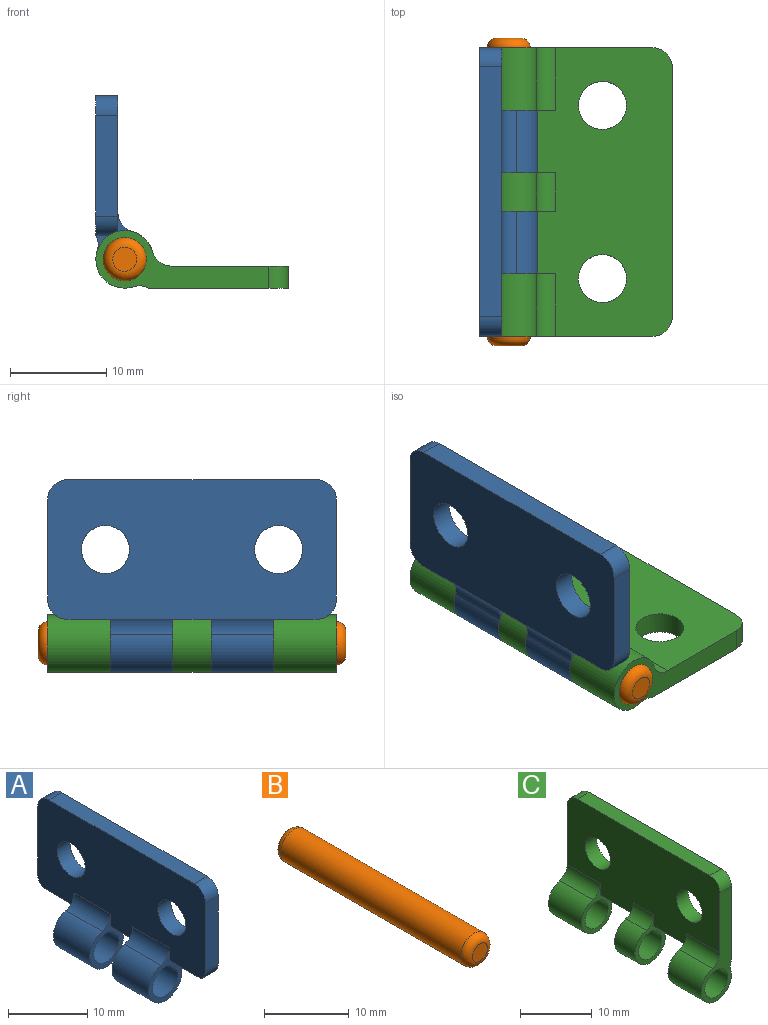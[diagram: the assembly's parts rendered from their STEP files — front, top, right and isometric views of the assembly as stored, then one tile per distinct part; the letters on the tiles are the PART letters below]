
ASSEMBLY  parts=3 mates=4
PART A: 29 faces, bbox 6x30x20 mm
  f0: plane 30x14.5mm, normal (1,0,0), area 392.3mm2, adj f2,f3,f8,f9,f10,f11,f20,f22
  f1: plane 30x14.08mm, normal (-1,0,0), area 355.9mm2, adj f8,f9,f10,f12,f13,f14,f15,f16
  f2: plane 4x1.34mm, normal (0,0,-1), area 5.4mm2, adj f0,f12,f13,f14
  f3: plane 4.5x1.34mm, normal (0,0,-1), area 6mm2, adj f0,f15,f16,f25
  f4: cylinder r=3mm len=6.5mm, axis (0,1,0), area 92.9mm2, adj f14,f18,f19,f20
  f5: cylinder r=2.25mm len=6.5mm, axis (0,1,0), area 91.9mm2, adj f14,f18
  f6: cylinder r=2.25mm len=6.5mm, axis (0,1,0), area 91.9mm2, adj f13,f16
  f7: cylinder r=3mm len=6.5mm, axis (0,1,0), area 92.9mm2, adj f13,f16,f21,f22
  f8: plane 10.5x2.3mm, normal (0,-1,0), area 24.1mm2, adj f0,f1,f23,f24
  f9: plane 10.5x2.3mm, normal (0,1,0), area 24.1mm2, adj f0,f1,f25,f26
  f10: plane 26x2.3mm, normal (0,0,1), area 59.8mm2, adj f0,f1,f23,f26
  f11: plane 4.5x1.34mm, normal (0,0,-1), area 6mm2, adj f0,f17,f18,f24
  f12: cylinder r=3mm len=4mm, axis (0,-1,0), area 4.2mm2, adj f1,f2,f13,f14
  f13: plane 7.83x6mm, normal (0,-1,0), area 13.7mm2, adj f1,f2,f6,f7,f12,f21,f22
  f14: plane 7.83x6mm, normal (0,1,0), area 13.7mm2, adj f1,f2,f4,f5,f12,f19,f20
  f15: cylinder r=3mm len=5.72mm, axis (0,1,0), area 5.7mm2, adj f1,f3,f16,f25
  f16: plane 7.83x6mm, normal (0,1,0), area 13.7mm2, adj f1,f3,f6,f7,f15,f21,f22
  f17: cylinder r=3mm len=5.72mm, axis (0,-1,0), area 5.7mm2, adj f1,f11,f18,f24
  f18: plane 7.83x6mm, normal (0,-1,0), area 13.7mm2, adj f1,f4,f5,f11,f17,f19,f20
  f19: cylinder r=2mm len=6.5mm, axis (0,1,0), area 17mm2, adj f1,f4,f14,f18
  f20: cylinder r=2mm len=6.5mm, axis (0,-1,0), area 10.6mm2, adj f0,f4,f14,f18
  f21: cylinder r=2mm len=6.5mm, axis (0,1,0), area 17mm2, adj f1,f7,f13,f16
  f22: cylinder r=2mm len=6.5mm, axis (0,-1,0), area 10.6mm2, adj f0,f7,f13,f16
  f23: cylinder r=2mm len=2.3mm, axis (1,0,0), area 7.2mm2, adj f0,f1,f8,f10
  f24: cylinder r=2mm len=2.3mm, axis (-1,0,0), area 6.3mm2, adj f0,f1,f8,f11,f17
  f25: cylinder r=2mm len=2.3mm, axis (1,0,0), area 6.3mm2, adj f0,f1,f3,f9,f15
  f26: cylinder r=2mm len=2.3mm, axis (-1,0,0), area 7.2mm2, adj f0,f1,f9,f10
  f27: cylinder r=2.5mm len=5mm, axis (-1,0,0), area 36.1mm2, adj f0,f1
  f28: cylinder r=2.5mm len=5mm, axis (-1,0,0), area 36.1mm2, adj f0,f1
PART B: 5 faces, bbox 4.9x32x4.9 mm
  f0: cylinder r=2.25mm len=30mm, axis (0,-1,0), area 424.1mm2, adj f3,f4
  f1: plane 2.5x2.5mm, normal (0,1,0), area 4.9mm2, adj f4
  f2: plane 2.5x2.5mm, normal (0,-1,0), area 4.9mm2, adj f3
  f3: torus R=1.25mm, axis (0,-1,0), area 18.6mm2, adj f0,f2
  f4: torus R=1.25mm, axis (0,-1,0), area 18.6mm2, adj f0,f1
PART C: 29 faces, bbox 6x30x20 mm
  f0: plane 30x14.5mm, normal (1,0,0), area 394mm2, adj f2,f9,f10,f11,f12,f20,f22,f23
  f1: plane 30x14.08mm, normal (-1,0,0), area 349mm2, adj f9,f10,f11,f13,f14,f15,f16,f17
  f2: plane 6.5x1.34mm, normal (0,0,-1), area 8.7mm2, adj f0,f16,f17,f18
  f3: cylinder r=3mm len=6.5mm, axis (0,1,0), area 92.9mm2, adj f10,f17,f19,f20
  f4: cylinder r=2.25mm len=6.5mm, axis (0,1,0), area 91.9mm2, adj f10,f17
  f5: cylinder r=3mm len=6mm, axis (0,1,0), area 57.2mm2, adj f15,f18,f21,f22
  f6: cylinder r=2.25mm len=4.5mm, axis (0,1,0), area 56.5mm2, adj f15,f18
  f7: cylinder r=3mm len=6.5mm, axis (0,1,0), area 92.9mm2, adj f9,f14,f24,f25
  f8: cylinder r=2.25mm len=6.5mm, axis (0,1,0), area 91.9mm2, adj f9,f14
  f9: plane 18x6mm, normal (0,-1,0), area 42.2mm2, adj f0,f1,f7,f8,f23,f24,f25
  f10: plane 18x6mm, normal (0,1,0), area 42.2mm2, adj f0,f1,f3,f4,f19,f20,f26
  f11: plane 26x2.3mm, normal (0,0,1), area 59.8mm2, adj f0,f1,f23,f26
  f12: plane 6.5x1.34mm, normal (0,0,-1), area 8.7mm2, adj f0,f13,f14,f15
  f13: cylinder r=3mm len=6.5mm, axis (0,1,0), area 6.8mm2, adj f1,f12,f14,f15
  f14: plane 7.83x6mm, normal (0,1,0), area 13.7mm2, adj f1,f7,f8,f12,f13,f24,f25
  f15: plane 7.83x6mm, normal (0,-1,0), area 13.7mm2, adj f1,f5,f6,f12,f13,f21,f22
  f16: cylinder r=3mm len=6.5mm, axis (0,-1,0), area 6.8mm2, adj f1,f2,f17,f18
  f17: plane 7.83x6mm, normal (0,-1,0), area 13.7mm2, adj f1,f2,f3,f4,f16,f19,f20
  f18: plane 7.83x6mm, normal (0,1,0), area 13.7mm2, adj f1,f2,f5,f6,f16,f21,f22
  f19: cylinder r=2mm len=6.5mm, axis (0,1,0), area 17mm2, adj f1,f3,f10,f17
  f20: cylinder r=2mm len=6.5mm, axis (0,-1,0), area 10.6mm2, adj f0,f3,f10,f17
  f21: cylinder r=2mm len=4mm, axis (0,1,0), area 10.5mm2, adj f1,f5,f15,f18
  f22: cylinder r=2mm len=4mm, axis (0,-1,0), area 6.5mm2, adj f0,f5,f15,f18
  f23: cylinder r=2mm len=2.3mm, axis (1,0,0), area 7.2mm2, adj f0,f1,f9,f11
  f24: cylinder r=2mm len=6.5mm, axis (0,1,0), area 17mm2, adj f1,f7,f9,f14
  f25: cylinder r=2mm len=6.5mm, axis (0,-1,0), area 10.6mm2, adj f0,f7,f9,f14
  f26: cylinder r=2mm len=2.3mm, axis (-1,0,0), area 7.2mm2, adj f0,f1,f10,f11
  f27: cylinder r=2.5mm len=5mm, axis (-1,0,0), area 36.1mm2, adj f0,f1
  f28: cylinder r=2.5mm len=5mm, axis (-1,0,0), area 36.1mm2, adj f0,f1
PLACE A rot(axis=(0,0,-1),180deg) t=(-133,0,-3)mm
PLACE B rot(axis=(0,1,0),90deg) t=(-3,0,-133)mm
PLACE C rot(axis=(0,1,0),90deg) t=(-3,0,-133)mm
MATE cylindrical A.f4 <-> B.f0  axis (0,-1,0) through (0,-8.5,0)mm
MATE planar B.f0 <-> C.f9  axis (0,-1,0) through (0,-15,0)mm
MATE planar A.f14 <-> C.f18  axis (0,-1,0) through (-0.14,2,0.26)mm
MATE cylindrical C.f3 <-> B.f0  axis (0,-1,0) through (0,-15,0)mm
